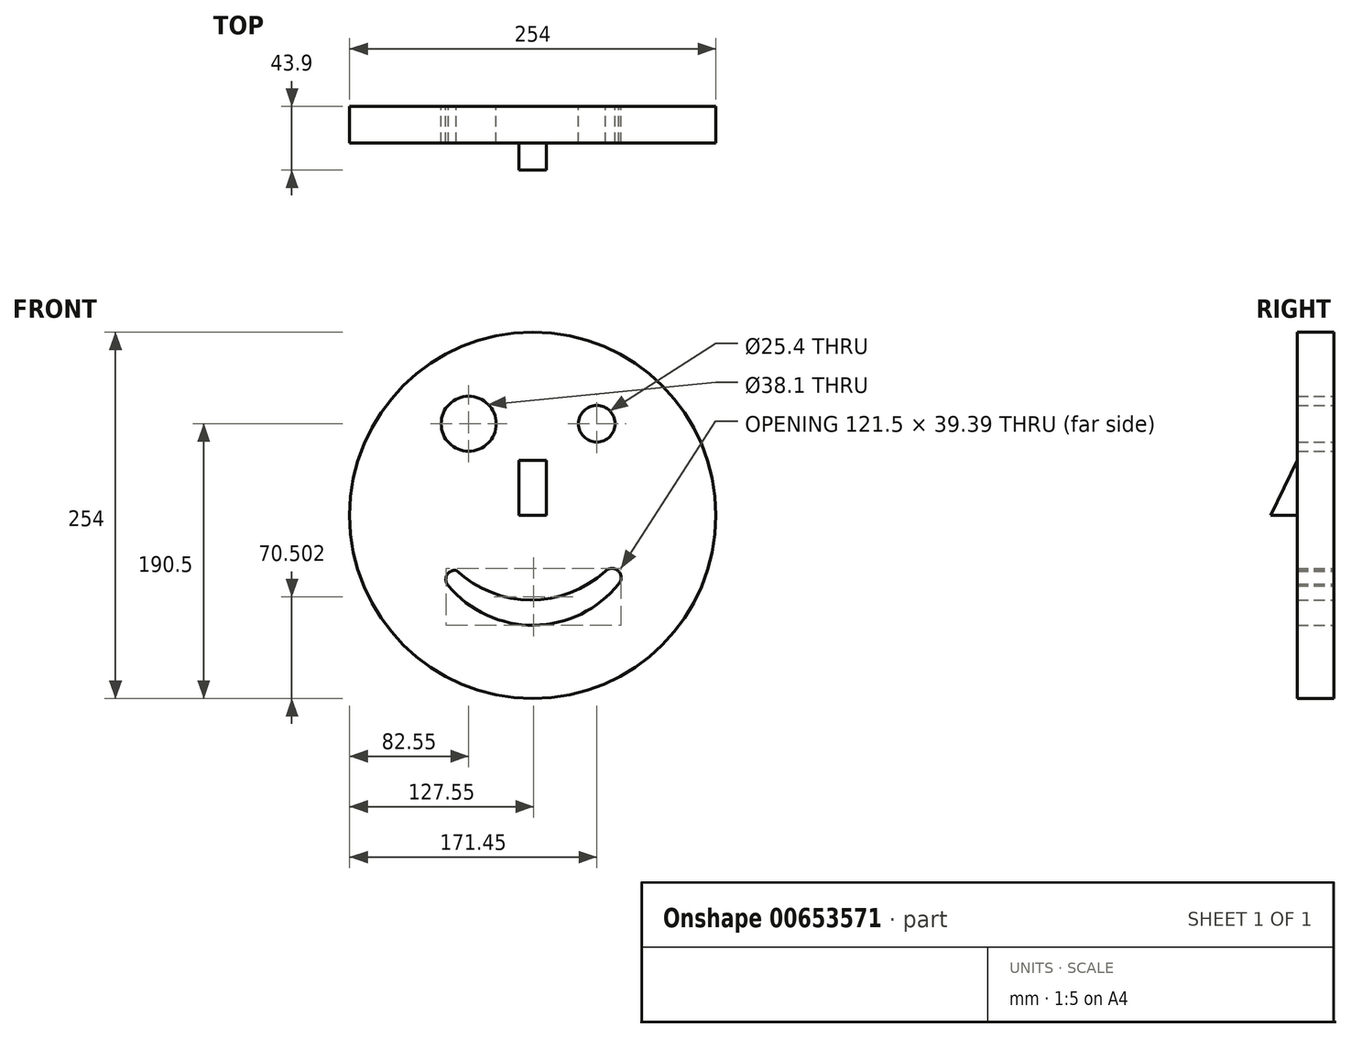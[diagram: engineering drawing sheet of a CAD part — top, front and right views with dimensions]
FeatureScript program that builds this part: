
annotation { "Feature Type Name" : "Feature", "Feature Type Description" : "" }
export const myFeature = defineFeature(function(context is Context, id is Id, definition is map)
    precondition{}
    {
        {
            var Q0;
            Q0=qCreatedBy(makeId("Front.planeOp"),FACE);
            var sketch = newSketch(context, id + "F0", { "sketchPlane" : qUnion([Q0])});
            skCircle(sketch, "E0", {"center": v(0, 0) * mm, "radius": 127 * mm});
            skLineSegment(sketch, "E1", {"start": v(0, 0) * mm, "end": v(0, 63.5) * mm});
            skLineSegment(sketch, "E2", {"start": v(0, 63.5) * mm, "end": v(-44.45, 63.5) * mm});
            skCircle(sketch, "E3", {"center": v(-44.45, 63.5) * mm, "radius": 19.05 * mm});
            skCircle(sketch, "E4", {"center": v(44.45, 63.5) * mm, "radius": 12.7 * mm});
            skArc(sketch, "E5", {"start": v(-58.54, -48.78) * mm, "mid": v(0.84, -76.2) * mm, "end": v(59.6, -47.48) * mm});
            skArc(sketch, "E6", {"start": v(-53.13, -38.13) * mm, "mid": v(-59.58, -41.56) * mm, "end": v(-58.54, -48.78) * mm});
            skArc(sketch, "E7", {"start": v(59.6, -47.48) * mm, "mid": v(59.37, -38.6) * mm, "end": v(50.49, -38.64) * mm});
            skArc(sketch, "E8", {"start": v(-53.13, -38.13) * mm, "mid": v(-1.42, -58.7) * mm, "end": v(50.49, -38.64) * mm});
            skSolve(sketch);
        }
        {
            var Q0;
            Q0=makeQuery(id+"F0.imprint","IMPRINT",FACE,{"disambiguationData":[TD([[makeQuery(id+"F0.imprint","IMPRINT",EDGE,{"derivedFrom":sQuery(id+"F0.wireOp",EDGE,"E0")}),1.0]])]});
            extrude(context, id + "F1", {"entities" : qUnion([Q0]), "depth" : 25.4 * mm, "offsetDistance" : 25.4 * mm});
        }
        {
            var Q0;
            Q0=qCreatedBy(makeId("Right.planeOp"),FACE);
            var sketch = newSketch(context, id + "F2", { "sketchPlane" : qUnion([Q0])});
            skLineSegment(sketch, "E9", {"start": v(0, 0) * mm, "end": v(-25.4, 0) * mm});
            skLineSegment(sketch, "E10", {"start": v(-25.4, 0) * mm, "end": v(-25.4, 38.1) * mm});
            skLineSegment(sketch, "E11", {"start": v(-25.4, 38.1) * mm, "end": v(-43.9, 0) * mm});
            skLineSegment(sketch, "E12", {"start": v(-43.9, 0) * mm, "end": v(-25.4, 0) * mm});
            skLineSegment(sketch, "E13", {"start": v(-25.4, 38.1) * mm, "end": v(-25.4, 0) * mm});
            skSolve(sketch);
        }
        {
            var Q0;
            Q0=makeQuery(id+"F2.imprint","IMPRINT",FACE,{"disambiguationData":[TD([[makeQuery(id+"F2.imprint","IMPRINT",EDGE,{"derivedFrom":sQuery(id+"F2.wireOp",EDGE,"E11")}),1.0]])]});
            extrude(context, id + "F3", {"entities" : qUnion([Q0]), "operationType" : NewBodyOperationType.ADD, "depth" : 19.05 * mm, "offsetDistance" : 25.4 * mm, "symmetric" : true});
        }
    });
